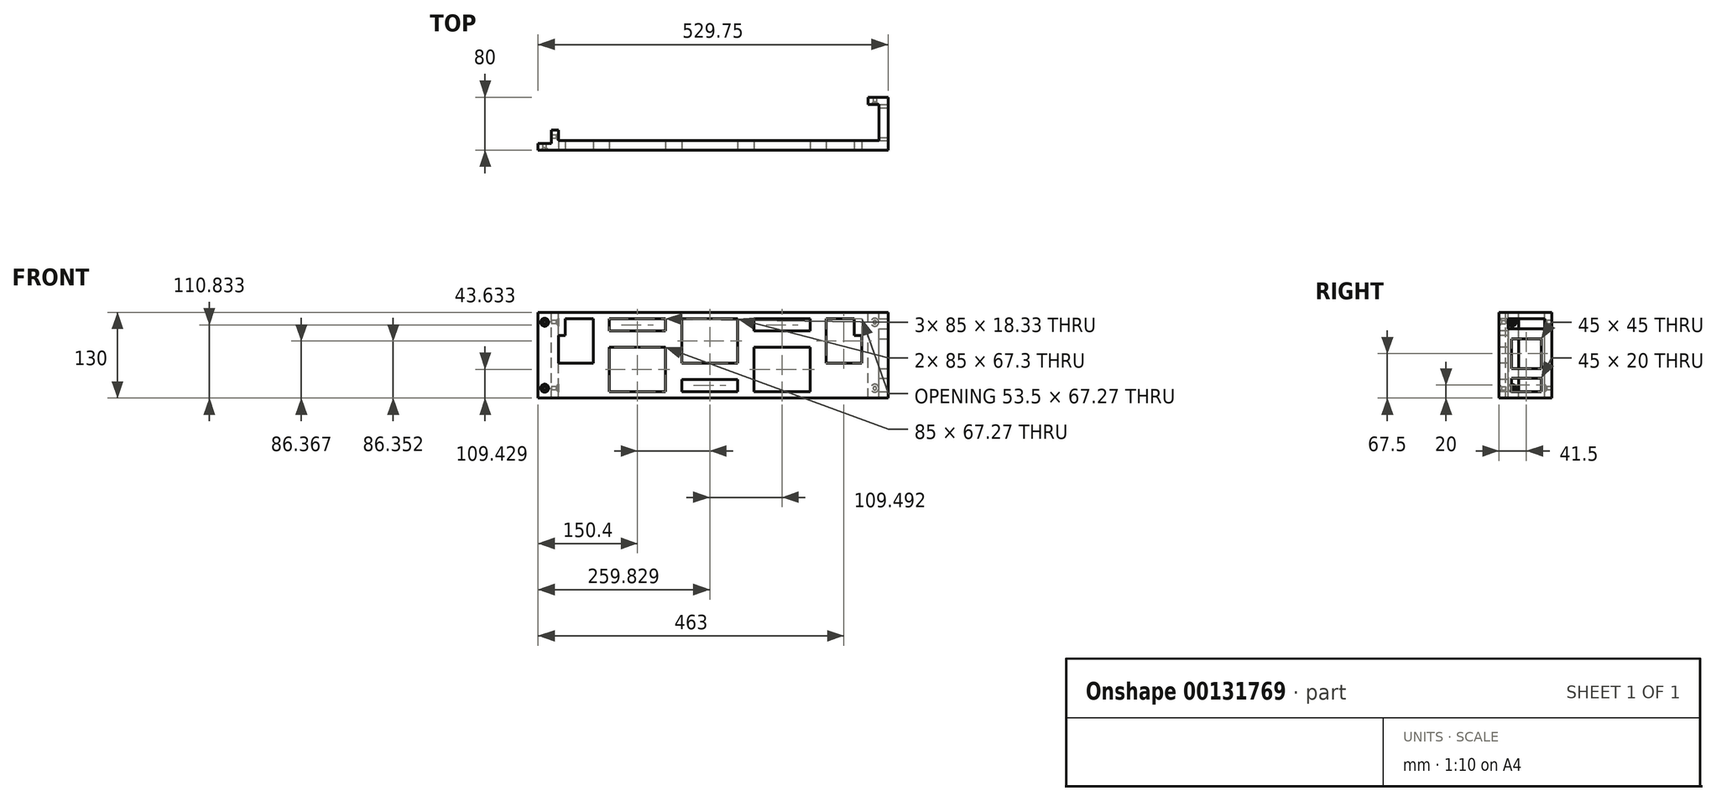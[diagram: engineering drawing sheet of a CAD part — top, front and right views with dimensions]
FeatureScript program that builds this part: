
annotation { "Feature Type Name" : "Feature", "Feature Type Description" : "" }
export const myFeature = defineFeature(function(context is Context, id is Id, definition is map)
    precondition{}
    {
        {
            var Q0;
            Q0=qCreatedBy(makeId("Front.planeOp"),FACE);
            var sketch = newSketch(context, id + "F0", { "sketchPlane" : qUnion([Q0])});
            skLineSegment(sketch, "E0.bottom", {"start": v(0, 0) * mm, "end": v(479.75, 0) * mm});
            skLineSegment(sketch, "E0.top", {"start": v(0, 130) * mm, "end": v(479.75, 130) * mm});
            skLineSegment(sketch, "E0.left", {"start": v(0, 0) * mm, "end": v(0, 130) * mm});
            skLineSegment(sketch, "E0.right", {"start": v(479.75, 0) * mm, "end": v(479.75, 130) * mm});
            skSolve(sketch);
        }
        {
            var Q0;
            Q0=makeQuery(id+"F0.imprint","IMPRINT",FACE,{"disambiguationData":[TD([[makeQuery(id+"F0.imprint","IMPRINT",EDGE,{"derivedFrom":sQuery(id+"F0.wireOp",EDGE,"E0.bottom")}),1.0]])]});
            extrude(context, id + "F1", {"entities" : qUnion([Q0]), "depth" : 14 * mm});
        }
        {
            var Q0;
            Q0=makeQuery(id+"F1.opExtrude","SWEPT_FACE",FACE,{"disambiguationData":[OSD([sQuery(id+"F0.wireOp",EDGE,"E0.top")])]});
            var sketch = newSketch(context, id + "F2", { "sketchPlane" : qUnion([Q0])});
            skLineSegment(sketch, "E1", {"start": v(0, -14) * mm, "end": v(-20, -14) * mm});
            skLineSegment(sketch, "E2", {"start": v(-20, -14) * mm, "end": v(-20, -4) * mm});
            skLineSegment(sketch, "E3", {"start": v(-20, -4) * mm, "end": v(0, -4) * mm});
            skLineSegment(sketch, "E4", {"start": v(0, -4) * mm, "end": v(0, -14) * mm});
            skLineSegment(sketch, "E5.bottom", {"start": v(479.75, -14) * mm, "end": v(509.75, -14) * mm});
            skLineSegment(sketch, "E5.top", {"start": v(479.75, 0) * mm, "end": v(495.75, 0) * mm});
            skLineSegment(sketch, "E5.left", {"start": v(479.75, -14) * mm, "end": v(479.75, 0) * mm});
            skLineSegment(sketch, "E6.top", {"start": v(509.75, 66) * mm, "end": v(479.75, 66) * mm});
            skLineSegment(sketch, "E6.left", {"start": v(509.75, -14) * mm, "end": v(509.75, 66) * mm});
            skLineSegment(sketch, "E6.right", {"start": v(495.75, 0) * mm, "end": v(495.75, 55) * mm});
            skLineSegment(sketch, "E7.top", {"start": v(495.75, 55) * mm, "end": v(479.75, 55) * mm});
            skLineSegment(sketch, "E7.right", {"start": v(479.75, 66) * mm, "end": v(479.75, 55) * mm});
            skSolve(sketch);
        }
        {
            var Q0;
            Q0=makeQuery(id+"F2.imprint","IMPRINT",FACE,{"disambiguationData":[TD([[makeQuery(id+"F2.imprint","IMPRINT",EDGE,{"derivedFrom":sQuery(id+"F2.wireOp",EDGE,"E5.bottom")}),1.0]])]});
            var Q1;
            Q1=makeQuery(id+"F2.imprint","IMPRINT",FACE,{"disambiguationData":[TD([[makeQuery(id+"F2.imprint","IMPRINT",EDGE,{"derivedFrom":sQuery(id+"F2.wireOp",EDGE,"E1")}),-1.0]])]});
            var Q2;
            Q2=makeQuery(id+"F2.imprint","IMPRINT",FACE,{"disambiguationData":[TD([[makeQuery(id+"F2.imprint","IMPRINT",EDGE,{"derivedFrom":sQuery(id+"F2.wireOp",EDGE,"E6.bottom")}),-1.0]])]});
            var Q3;
            Q3=makeQuery(id+"F1.opExtrude","SWEPT_FACE",FACE,{"disambiguationData":[OSD([sQuery(id+"F0.wireOp",EDGE,"E0.bottom")])]});
            extrude(context, id + "F3", {"entities" : qUnion([Q0, Q1, Q2]), "operationType" : NewBodyOperationType.ADD, "endBound" : BoundingType.UP_TO_SURFACE, "oppositeDirection" : true, "endBoundEntityFace" : qUnion([Q3]), "depth" : 25 * mm});
        }
        {
            var Q0;
            Q0=makeQuery(id+"F3.boolean.opBoolean","MERGE",FACE,{"derivedFrom":[makeQuery(id+"F1.opExtrude","SWEPT_FACE",FACE,{"disambiguationData":[OSD([sQuery(id+"F0.wireOp",EDGE,"E0.top")])]}),makeQuery(id+"F3.opExtrude","CAP_FACE",FACE,{"disambiguationData":[OSD([sQuery(id+"F2.wireOp",EDGE,"E1"),sQuery(id+"F2.wireOp",EDGE,"E2"),sQuery(id+"F2.wireOp",EDGE,"E3"),sQuery(id+"F2.wireOp",EDGE,"E4")])],"isStart":true}),makeQuery(id+"F3.opExtrude","CAP_FACE",FACE,{"disambiguationData":[OSD([sQuery(id+"F2.wireOp",EDGE,"E5.bottom"),sQuery(id+"F2.wireOp",EDGE,"E5.top"),sQuery(id+"F2.wireOp",EDGE,"E5.left"),sQuery(id+"F2.wireOp",EDGE,"E5.right")])],"isStart":true})]});
            var sketch = newSketch(context, id + "F4", { "sketchPlane" : qUnion([Q0])});
            skLineSegment(sketch, "E8", {"start": v(0, 0) * mm, "end": v(0, 16) * mm});
            skLineSegment(sketch, "E9", {"start": v(0, 16) * mm, "end": v(11, 16) * mm});
            skLineSegment(sketch, "E10", {"start": v(11, 16) * mm, "end": v(11, 0) * mm});
            skLineSegment(sketch, "E11", {"start": v(11, 0) * mm, "end": v(0, 0) * mm});
            skSolve(sketch);
        }
        {
            var Q0;
            Q0=makeQuery(id+"F4.imprint","IMPRINT",FACE,{"disambiguationData":[TD([[makeQuery(id+"F4.imprint","IMPRINT",EDGE,{"derivedFrom":sQuery(id+"F4.wireOp",EDGE,"g1681GE8-kr8q-vAWY-LNZA-GesWc0OhcODc.bottom")}),1.0]])]});
            var Q1;
            Q1=makeQuery(id+"F4.imprint","IMPRINT",FACE,{"disambiguationData":[TD([[makeQuery(id+"F4.imprint","IMPRINT",EDGE,{"derivedFrom":sQuery(id+"F4.wireOp",EDGE,"E8")}),-1.0]])]});
            var Q2;
            {var subQ0=sQuery(id+"F0.wireOp",EDGE,"E0.bottom");Q2=makeQuery(id+"F3.boolean.opBoolean","MERGE",FACE,{"derivedFrom":[makeQuery(id+"F1.opExtrude","SWEPT_FACE",FACE,{"disambiguationData":[OSD([subQ0])]}),makeQuery(id+"F3.opExtrude","CAP_FACE",FACE,{"disambiguationData":[OSD([subQ0]),ownerDisambiguation([makeQuery(id+"F3.opExtrude","SWEPT_BODY",BODY,{"disambiguationData":[OSD([sQuery(id+"F2.wireOp",EDGE,"E1"),sQuery(id+"F2.wireOp",EDGE,"E2"),sQuery(id+"F2.wireOp",EDGE,"E3"),sQuery(id+"F2.wireOp",EDGE,"E4")])]})])],"isStart":false}),makeQuery(id+"F3.opExtrude","CAP_FACE",FACE,{"disambiguationData":[OSD([subQ0]),ownerDisambiguation([makeQuery(id+"F3.opExtrude","SWEPT_BODY",BODY,{"disambiguationData":[OSD([sQuery(id+"F2.wireOp",EDGE,"E5.bottom"),sQuery(id+"F2.wireOp",EDGE,"E5.top"),sQuery(id+"F2.wireOp",EDGE,"E5.left"),sQuery(id+"F2.wireOp",EDGE,"E5.right")])]})])],"isStart":false})]});}
            extrude(context, id + "F5", {"entities" : qUnion([Q0, Q1]), "operationType" : NewBodyOperationType.ADD, "endBound" : BoundingType.UP_TO_SURFACE, "oppositeDirection" : true, "endBoundEntityFace" : qUnion([Q2]), "depth" : 25 * mm});
        }
        {
            var Q0;
            Q0=makeQuery(id+"F3.boolean.opBoolean","MERGE",FACE,{"derivedFrom":[makeQuery(id+"F1.opExtrude","CAP_FACE",FACE,{"disambiguationData":[OSD([sQuery(id+"F0.wireOp",EDGE,"E0.bottom"),sQuery(id+"F0.wireOp",EDGE,"E0.top"),sQuery(id+"F0.wireOp",EDGE,"E0.left"),sQuery(id+"F0.wireOp",EDGE,"E0.right")])],"isStart":false}),makeQuery(id+"F3.opExtrude","SWEPT_FACE",FACE,{"disambiguationData":[OSD([sQuery(id+"F2.wireOp",EDGE,"E1")])]}),makeQuery(id+"F3.opExtrude","SWEPT_FACE",FACE,{"disambiguationData":[OSD([sQuery(id+"F2.wireOp",EDGE,"E5.bottom")])]})]});
            var sketch = newSketch(context, id + "F6", { "sketchPlane" : qUnion([Q0])});
            skLineSegment(sketch, "E12.0", {"start": v(21, 95) * mm, "end": v(21, 120) * mm});
            skLineSegment(sketch, "E12.2", {"start": v(469.75, 95) * mm, "end": v(469.75, 52.73) * mm});
            skLineSegment(sketch, "E12.3", {"start": v(458.75, 95) * mm, "end": v(469.75, 95) * mm});
            skLineSegment(sketch, "E12.4", {"start": v(458.75, 95) * mm, "end": v(458.75, 120) * mm});
            skLineSegment(sketch, "E12.5", {"start": v(458.75, 10) * mm, "end": v(458.75, 28.33) * mm});
            skLineSegment(sketch, "E12.6", {"start": v(21, 120) * mm, "end": v(458.75, 120) * mm});
            skLineSegment(sketch, "E12.7", {"start": v(458.75, 10) * mm, "end": v(21, 10) * mm});
            skLineSegment(sketch, "E12.8", {"start": v(21, 10) * mm, "end": v(21, 28.33) * mm});
            skLineSegment(sketch, "E12.11", {"start": v(11, 95) * mm, "end": v(21, 95) * mm});
            skLineSegment(sketch, "E13", {"start": v(130.4, 120) * mm, "end": v(130.4, 10) * mm});
            skLineSegment(sketch, "E14", {"start": v(239.8, 120) * mm, "end": v(239.8, 10) * mm});
            skLineSegment(sketch, "E15", {"start": v(349.35, 120) * mm, "end": v(349.35, 10) * mm});
            skLineSegment(sketch, "E16", {"start": v(21, 10) * mm, "end": v(130.4, 120) * mm, "construction": true});
            skLineSegment(sketch, "E17", {"start": v(130.4, 120) * mm, "end": v(239.8, 10) * mm, "construction": true});
            skLineSegment(sketch, "E18", {"start": v(239.8, 10) * mm, "end": v(349.35, 120) * mm, "construction": true});
            skLineSegment(sketch, "E19", {"start": v(349.35, 120) * mm, "end": v(458.75, 10) * mm, "construction": true});
            skLineSegment(sketch, "E20.bottom", {"start": v(87.9, 77.27) * mm, "end": v(172.9, 77.27) * mm});
            skLineSegment(sketch, "E20.top", {"start": v(87.9, 10) * mm, "end": v(172.9, 10) * mm});
            skLineSegment(sketch, "E20.left", {"start": v(87.9, 77.27) * mm, "end": v(87.9, 10) * mm});
            skLineSegment(sketch, "E20.right", {"start": v(172.9, 77.27) * mm, "end": v(172.9, 10) * mm});
            skLineSegment(sketch, "E21.bottom", {"start": v(282.33, 52.7) * mm, "end": v(197.33, 52.7) * mm});
            skLineSegment(sketch, "E21.top", {"start": v(282.33, 120) * mm, "end": v(197.33, 120) * mm});
            skLineSegment(sketch, "E21.left", {"start": v(282.33, 52.7) * mm, "end": v(282.33, 120) * mm});
            skLineSegment(sketch, "E21.right", {"start": v(197.33, 52.7) * mm, "end": v(197.33, 120) * mm});
            skLineSegment(sketch, "E22.bottom", {"start": v(306.82, 77.3) * mm, "end": v(391.82, 77.3) * mm});
            skLineSegment(sketch, "E22.top", {"start": v(306.82, 10) * mm, "end": v(391.82, 10) * mm});
            skLineSegment(sketch, "E22.left", {"start": v(306.82, 77.3) * mm, "end": v(306.82, 10) * mm});
            skLineSegment(sketch, "E22.right", {"start": v(391.82, 77.3) * mm, "end": v(391.82, 10) * mm});
            skLineSegment(sketch, "E23.bottom", {"start": v(63.5, 120) * mm, "end": v(21, 120) * mm});
            skLineSegment(sketch, "E23.top", {"start": v(63.5, 52.73) * mm, "end": v(21, 52.73) * mm});
            skLineSegment(sketch, "E23.left", {"start": v(63.5, 120) * mm, "end": v(63.5, 52.73) * mm});
            skLineSegment(sketch, "E23.right", {"start": v(21, 120) * mm, "end": v(21, 95) * mm});
            skLineSegment(sketch, "E24.bottom", {"start": v(458.75, 120) * mm, "end": v(416.25, 120) * mm});
            skLineSegment(sketch, "E24.top", {"start": v(469.75, 52.73) * mm, "end": v(416.25, 52.73) * mm});
            skLineSegment(sketch, "E24.left", {"start": v(458.75, 120) * mm, "end": v(458.75, 95) * mm});
            skLineSegment(sketch, "E24.right", {"start": v(416.25, 120) * mm, "end": v(416.25, 52.73) * mm});
            skLineSegment(sketch, "E25", {"start": v(21, 52.73) * mm, "end": v(11, 52.73) * mm});
            skLineSegment(sketch, "E26.bottom", {"start": v(87.9, 120) * mm, "end": v(172.9, 120) * mm});
            skLineSegment(sketch, "E26.top", {"start": v(87.9, 101.67) * mm, "end": v(172.9, 101.67) * mm});
            skLineSegment(sketch, "E26.left", {"start": v(87.9, 120) * mm, "end": v(87.9, 101.67) * mm});
            skLineSegment(sketch, "E26.right", {"start": v(172.9, 120) * mm, "end": v(172.9, 101.67) * mm});
            skLineSegment(sketch, "E27.bottom", {"start": v(197.33, 10) * mm, "end": v(282.33, 10) * mm});
            skLineSegment(sketch, "E27.top", {"start": v(197.33, 28.33) * mm, "end": v(282.33, 28.33) * mm});
            skLineSegment(sketch, "E27.left", {"start": v(197.33, 10) * mm, "end": v(197.33, 28.33) * mm});
            skLineSegment(sketch, "E27.right", {"start": v(282.33, 10) * mm, "end": v(282.33, 28.33) * mm});
            skLineSegment(sketch, "E28.bottom", {"start": v(306.82, 120) * mm, "end": v(391.82, 120) * mm});
            skLineSegment(sketch, "E28.top", {"start": v(306.82, 101.67) * mm, "end": v(391.82, 101.67) * mm});
            skLineSegment(sketch, "E28.left", {"start": v(306.82, 120) * mm, "end": v(306.82, 101.67) * mm});
            skLineSegment(sketch, "E28.right", {"start": v(391.82, 120) * mm, "end": v(391.82, 101.67) * mm});
            skLineSegment(sketch, "E29.bottom", {"start": v(21, 10) * mm, "end": v(63.5, 10) * mm});
            skLineSegment(sketch, "E29.top", {"start": v(21, 28.33) * mm, "end": v(63.5, 28.33) * mm});
            skLineSegment(sketch, "E29.right", {"start": v(63.5, 10) * mm, "end": v(63.5, 28.33) * mm});
            skLineSegment(sketch, "E30.bottom", {"start": v(458.75, 10) * mm, "end": v(416.25, 10) * mm});
            skLineSegment(sketch, "E30.top", {"start": v(458.75, 28.33) * mm, "end": v(416.25, 28.33) * mm});
            skLineSegment(sketch, "E30.right", {"start": v(416.25, 10) * mm, "end": v(416.25, 28.33) * mm});
            skLineSegment(sketch, "E31.trimOffspring", {"start": v(11, 95) * mm, "end": v(11, 52.73) * mm});
            skPoint(sketch, "E32.orphan", {"position": v(11, 0) * mm});
            skSolve(sketch);
        }
        {
            var Q0;
            {var subQ0=sQuery(id+"F6.wireOp",EDGE,"E12.11");Q0=makeQuery(id+"F6.imprint","IMPRINT",FACE,{"disambiguationData":[TD([[makeQuery(id+"F6.imprint","IMPRINT",EDGE,{"derivedFrom":subQ0}),-1.0]])]});}
            var Q1;
            Q1=makeQuery(id+"F6.imprint","IMPRINT",FACE,{"disambiguationData":[TD([[makeQuery(id+"F6.imprint","IMPRINT",EDGE,{"derivedFrom":sQuery(id+"F6.wireOp",EDGE,"E29.bottom")}),1.0]])]});
            var Q2;
            {var subQ5=sQuery(id+"F6.wireOp",EDGE,"E20.left");Q2=makeQuery(id+"F6.imprint","IMPRINT",FACE,{"disambiguationData":[TD([[makeQuery(id+"F6.imprint","IMPRINT",EDGE,{"derivedFrom":subQ5}),1.0]])]});}
            var Q3;
            {var subQ5=sQuery(id+"F6.wireOp",EDGE,"E20.right");Q3=makeQuery(id+"F6.imprint","IMPRINT",FACE,{"disambiguationData":[TD([[makeQuery(id+"F6.imprint","IMPRINT",EDGE,{"derivedFrom":subQ5}),-1.0]])]});}
            var Q4;
            {var subQ5=sQuery(id+"F6.wireOp",EDGE,"E26.left");Q4=makeQuery(id+"F6.imprint","IMPRINT",FACE,{"disambiguationData":[TD([[makeQuery(id+"F6.imprint","IMPRINT",EDGE,{"derivedFrom":subQ5}),1.0]])]});}
            var Q5;
            {var subQ5=sQuery(id+"F6.wireOp",EDGE,"E26.right");Q5=makeQuery(id+"F6.imprint","IMPRINT",FACE,{"disambiguationData":[TD([[makeQuery(id+"F6.imprint","IMPRINT",EDGE,{"derivedFrom":subQ5}),-1.0]])]});}
            var Q6;
            {var subQ5=sQuery(id+"F6.wireOp",EDGE,"E21.right");Q6=makeQuery(id+"F6.imprint","IMPRINT",FACE,{"disambiguationData":[TD([[makeQuery(id+"F6.imprint","IMPRINT",EDGE,{"derivedFrom":subQ5}),-1.0]])]});}
            var Q7;
            {var subQ5=sQuery(id+"F6.wireOp",EDGE,"E21.left");Q7=makeQuery(id+"F6.imprint","IMPRINT",FACE,{"disambiguationData":[TD([[makeQuery(id+"F6.imprint","IMPRINT",EDGE,{"derivedFrom":subQ5}),1.0]])]});}
            var Q8;
            {var subQ5=sQuery(id+"F6.wireOp",EDGE,"E27.left");Q8=makeQuery(id+"F6.imprint","IMPRINT",FACE,{"disambiguationData":[TD([[makeQuery(id+"F6.imprint","IMPRINT",EDGE,{"derivedFrom":subQ5}),-1.0]])]});}
            var Q9;
            {var subQ5=sQuery(id+"F6.wireOp",EDGE,"E27.right");Q9=makeQuery(id+"F6.imprint","IMPRINT",FACE,{"disambiguationData":[TD([[makeQuery(id+"F6.imprint","IMPRINT",EDGE,{"derivedFrom":subQ5}),1.0]])]});}
            var Q10;
            {var subQ5=sQuery(id+"F6.wireOp",EDGE,"E22.left");Q10=makeQuery(id+"F6.imprint","IMPRINT",FACE,{"disambiguationData":[TD([[makeQuery(id+"F6.imprint","IMPRINT",EDGE,{"derivedFrom":subQ5}),1.0]])]});}
            var Q11;
            {var subQ5=sQuery(id+"F6.wireOp",EDGE,"E22.right");Q11=makeQuery(id+"F6.imprint","IMPRINT",FACE,{"disambiguationData":[TD([[makeQuery(id+"F6.imprint","IMPRINT",EDGE,{"derivedFrom":subQ5}),-1.0]])]});}
            var Q12;
            {var subQ5=sQuery(id+"F6.wireOp",EDGE,"E28.right");Q12=makeQuery(id+"F6.imprint","IMPRINT",FACE,{"disambiguationData":[TD([[makeQuery(id+"F6.imprint","IMPRINT",EDGE,{"derivedFrom":subQ5}),-1.0]])]});}
            var Q13;
            {var subQ5=sQuery(id+"F6.wireOp",EDGE,"E28.left");Q13=makeQuery(id+"F6.imprint","IMPRINT",FACE,{"disambiguationData":[TD([[makeQuery(id+"F6.imprint","IMPRINT",EDGE,{"derivedFrom":subQ5}),1.0]])]});}
            var Q14;
            {var subQ0=sQuery(id+"F6.wireOp",EDGE,"E12.3");Q14=makeQuery(id+"F6.imprint","IMPRINT",FACE,{"disambiguationData":[TD([[makeQuery(id+"F6.imprint","IMPRINT",EDGE,{"derivedFrom":subQ0}),-1.0]])]});}
            var Q15;
            Q15=makeQuery(id+"F6.imprint","IMPRINT",FACE,{"disambiguationData":[TD([[makeQuery(id+"F6.imprint","IMPRINT",EDGE,{"derivedFrom":sQuery(id+"F6.wireOp",EDGE,"E30.bottom")}),-1.0]])]});
            extrude(context, id + "F7", {"entities" : qUnion([Q0, Q1, Q2, Q3, Q4, Q5, Q6, Q7, Q8, Q9, Q10, Q11, Q12, Q13, Q14, Q15]), "operationType" : NewBodyOperationType.REMOVE, "oppositeDirection" : true, "depth" : 25 * mm});
        }
        {
            var Q0;
            Q0=makeQuery(id+"F3.opExtrude","SWEPT_FACE",FACE,{"disambiguationData":[OSD([sQuery(id+"F2.wireOp",EDGE,"E3")])]});
            var sketch = newSketch(context, id + "F8", { "sketchPlane" : qUnion([Q0])});
            skCircle(sketch, "E33", {"center": v(10, 115) * mm, "radius": 2.5 * mm});
            skCircle(sketch, "E34", {"center": v(10, 15) * mm, "radius": 2.5 * mm});
            skSolve(sketch);
        }
        {
            var Q0;
            Q0 = qSketchRegion(id + "F8", true);
            extrude(context, id + "F9", {"entities" : qUnion([Q0]), "operationType" : NewBodyOperationType.REMOVE, "oppositeDirection" : true, "depth" : 25 * mm});
        }
        {
            var Q0;
            Q0=makeQuery(id+"F3.opExtrude","SWEPT_FACE",FACE,{"disambiguationData":[OSD([sQuery(id+"F2.wireOp",EDGE,"E7.top")])]});
            var sketch = newSketch(context, id + "F10", { "sketchPlane" : qUnion([Q0])});
            skCircle(sketch, "E35", {"center": v(489.75, 15) * mm, "radius": 2.5 * mm});
            skCircle(sketch, "E36", {"center": v(489.75, 115) * mm, "radius": 2.5 * mm});
            skSolve(sketch);
        }
        {
            var Q0;
            Q0 = qSketchRegion(id + "F10", true);
            extrude(context, id + "F11", {"entities" : qUnion([Q0]), "operationType" : NewBodyOperationType.REMOVE, "endBound" : BoundingType.THROUGH_ALL, "oppositeDirection" : true, "depth" : 25 * mm, "hasSecondDirection" : true, "secondDirectionOppositeDirection" : false, "secondDirectionDepth" : 25 * mm});
        }
        {
            var Q0;
            Q0=makeQuery(id+"F5.boolean.opBoolean","MERGE",FACE,{"derivedFrom":[makeQuery(id+"F1.opExtrude","SWEPT_FACE",FACE,{"disambiguationData":[OSD([sQuery(id+"F0.wireOp",EDGE,"E0.left")])]}),makeQuery(id+"F5.opExtrude","SWEPT_FACE",FACE,{"disambiguationData":[OSD([sQuery(id+"F4.wireOp",EDGE,"E8")])]})]});
            var sketch = newSketch(context, id + "F12", { "sketchPlane" : qUnion([Q0])});
            skCircle(sketch, "E37", {"center": v(-6, 15) * mm, "radius": 2.5 * mm});
            skCircle(sketch, "E38", {"center": v(-6, 115) * mm, "radius": 2.5 * mm});
            skSolve(sketch);
        }
        {
            var Q0;
            Q0 = qSketchRegion(id + "F12", true);
            extrude(context, id + "F13", {"entities" : qUnion([Q0]), "operationType" : NewBodyOperationType.REMOVE, "oppositeDirection" : true, "depth" : 25 * mm});
        }
        {
            var Q0;
            Q0=makeQuery(id+"F11.boolean.opBoolean","INTERSECT",EDGE,{"derivedFrom":[makeQuery(id+"F3.opExtrude","SWEPT_FACE",FACE,{"disambiguationData":[OSD([sQuery(id+"F2.wireOp",EDGE,"E7.top")])]}),makeQuery(id+"F11.opExtrude","SWEPT_FACE",FACE,{"disambiguationData":[OSD([sQuery(id+"F10.wireOp",EDGE,"E35")])]})]});
            var Q1;
            Q1=makeQuery(id+"F11.boolean.opBoolean","INTERSECT",EDGE,{"derivedFrom":[makeQuery(id+"F3.opExtrude","SWEPT_FACE",FACE,{"disambiguationData":[OSD([sQuery(id+"F2.wireOp",EDGE,"E7.top")])]}),makeQuery(id+"F11.opExtrude","SWEPT_FACE",FACE,{"disambiguationData":[OSD([sQuery(id+"F10.wireOp",EDGE,"E36")])]})]});
            var Q2;
            Q2=makeQuery(id+"F9.boolean.opBoolean","INTERSECT",EDGE,{"derivedFrom":[makeQuery(id+"F3.boolean.opBoolean","MERGE",FACE,{"derivedFrom":[makeQuery(id+"F1.opExtrude","CAP_FACE",FACE,{"disambiguationData":[OSD([sQuery(id+"F0.wireOp",EDGE,"E0.bottom"),sQuery(id+"F0.wireOp",EDGE,"E0.top"),sQuery(id+"F0.wireOp",EDGE,"E0.left"),sQuery(id+"F0.wireOp",EDGE,"E0.right")])],"isStart":false}),makeQuery(id+"F3.opExtrude","SWEPT_FACE",FACE,{"disambiguationData":[OSD([sQuery(id+"F2.wireOp",EDGE,"E1")])]}),makeQuery(id+"F3.opExtrude","SWEPT_FACE",FACE,{"disambiguationData":[OSD([sQuery(id+"F2.wireOp",EDGE,"E5.bottom")])]})]}),makeQuery(id+"F9.opExtrude","SWEPT_FACE",FACE,{"disambiguationData":[OSD([sQuery(id+"F8.wireOp",EDGE,"E34")])]})]});
            var Q3;
            Q3=makeQuery(id+"F9.boolean.opBoolean","INTERSECT",EDGE,{"derivedFrom":[makeQuery(id+"F3.boolean.opBoolean","MERGE",FACE,{"derivedFrom":[makeQuery(id+"F1.opExtrude","CAP_FACE",FACE,{"disambiguationData":[OSD([sQuery(id+"F0.wireOp",EDGE,"E0.bottom"),sQuery(id+"F0.wireOp",EDGE,"E0.top"),sQuery(id+"F0.wireOp",EDGE,"E0.left"),sQuery(id+"F0.wireOp",EDGE,"E0.right")])],"isStart":false}),makeQuery(id+"F3.opExtrude","SWEPT_FACE",FACE,{"disambiguationData":[OSD([sQuery(id+"F2.wireOp",EDGE,"E1")])]}),makeQuery(id+"F3.opExtrude","SWEPT_FACE",FACE,{"disambiguationData":[OSD([sQuery(id+"F2.wireOp",EDGE,"E5.bottom")])]})]}),makeQuery(id+"F9.opExtrude","SWEPT_FACE",FACE,{"disambiguationData":[OSD([sQuery(id+"F8.wireOp",EDGE,"E33")])]})]});
            var Q4;
            Q4=makeQuery(id+"F13.boolean.opBoolean","INTERSECT",EDGE,{"derivedFrom":[makeQuery(id+"F7.boolean.opBoolean","MERGE",FACE,{"derivedFrom":[makeQuery(id+"F5.opExtrude","SWEPT_FACE",FACE,{"disambiguationData":[OSD([sQuery(id+"F4.wireOp",EDGE,"E10")])]}),makeQuery(id+"F7.opExtrude","SWEPT_FACE",FACE,{"disambiguationData":[OSD([sQuery(id+"F6.wireOp",EDGE,"E31.trimOffspring")])]})]}),makeQuery(id+"F13.opExtrude","SWEPT_FACE",FACE,{"disambiguationData":[OSD([sQuery(id+"F12.wireOp",EDGE,"E37")])]})]});
            var Q5;
            Q5=makeQuery(id+"F13.boolean.opBoolean","INTERSECT",EDGE,{"derivedFrom":[makeQuery(id+"F7.boolean.opBoolean","MERGE",FACE,{"derivedFrom":[makeQuery(id+"F5.opExtrude","SWEPT_FACE",FACE,{"disambiguationData":[OSD([sQuery(id+"F4.wireOp",EDGE,"E10")])]}),makeQuery(id+"F7.opExtrude","SWEPT_FACE",FACE,{"disambiguationData":[OSD([sQuery(id+"F6.wireOp",EDGE,"E31.trimOffspring")])]})]}),makeQuery(id+"F13.opExtrude","SWEPT_FACE",FACE,{"disambiguationData":[OSD([sQuery(id+"F12.wireOp",EDGE,"E38")])]})]});
            chamfer(context, id + "F14", {"entities" : qUnion([Q0, Q1, Q2, Q3, Q4, Q5]), "width" : 3.5 * mm, "tangentPropagation" : true});
        }
        {
            var Q0;
            Q0=makeQuery(id+"F3.opExtrude","SWEPT_FACE",FACE,{"disambiguationData":[OSD([sQuery(id+"F2.wireOp",EDGE,"E6.left")])]});
            var sketch = newSketch(context, id + "F15", { "sketchPlane" : qUnion([Q0])});
            skLineSegment(sketch, "E39.bottom", {"start": v(5, 10) * mm, "end": v(50, 10) * mm});
            skLineSegment(sketch, "E39.top", {"start": v(5, 90) * mm, "end": v(50, 90) * mm});
            skLineSegment(sketch, "E39.left", {"start": v(5, 10) * mm, "end": v(5, 90) * mm});
            skLineSegment(sketch, "E39.right", {"start": v(50, 10) * mm, "end": v(50, 90) * mm});
            skLineSegment(sketch, "E40.bottom", {"start": v(0, 120) * mm, "end": v(55, 120) * mm});
            skLineSegment(sketch, "E40.top", {"start": v(0, 105) * mm, "end": v(55, 105) * mm});
            skLineSegment(sketch, "E40.left", {"start": v(0, 120) * mm, "end": v(0, 105) * mm});
            skLineSegment(sketch, "E40.right", {"start": v(55, 120) * mm, "end": v(55, 105) * mm});
            skLineSegment(sketch, "E41.0", {"start": v(0, 0) * mm, "end": v(0, 130) * mm, "construction": true});
            skLineSegment(sketch, "E42.0", {"start": v(55, 15) * mm, "end": v(55, 15) * mm});
            skLineSegment(sketch, "E43.0", {"start": v(55, 0) * mm, "end": v(55, 130) * mm, "construction": true});
            skLineSegment(sketch, "E44", {"start": v(5, 30) * mm, "end": v(50, 30) * mm});
            skLineSegment(sketch, "E45", {"start": v(5, 45) * mm, "end": v(50, 45) * mm});
            skSolve(sketch);
        }
        {
            var Q0;
            Q0=makeQuery(id+"F15.imprint","IMPRINT",FACE,{"disambiguationData":[TD([[makeQuery(id+"F15.imprint","IMPRINT",EDGE,{"derivedFrom":sQuery(id+"F15.wireOp",EDGE,"E39.bottom")}),1.0]])]});
            var Q1;
            Q1=makeQuery(id+"F15.imprint","IMPRINT",FACE,{"disambiguationData":[TD([[makeQuery(id+"F15.imprint","IMPRINT",EDGE,{"derivedFrom":sQuery(id+"F15.wireOp",EDGE,"E40.bottom")}),-1.0]])]});
            var Q2;
            {var subQ0=sQuery(id+"F15.wireOp",EDGE,"E39.top");Q2=makeQuery(id+"F15.imprint","IMPRINT",FACE,{"disambiguationData":[TD([[makeQuery(id+"F15.imprint","IMPRINT",EDGE,{"derivedFrom":subQ0}),-1.0]])]});}
            extrude(context, id + "F16", {"entities" : qUnion([Q0, Q1, Q2]), "operationType" : NewBodyOperationType.REMOVE, "oppositeDirection" : true, "depth" : 25 * mm});
        }
    });
